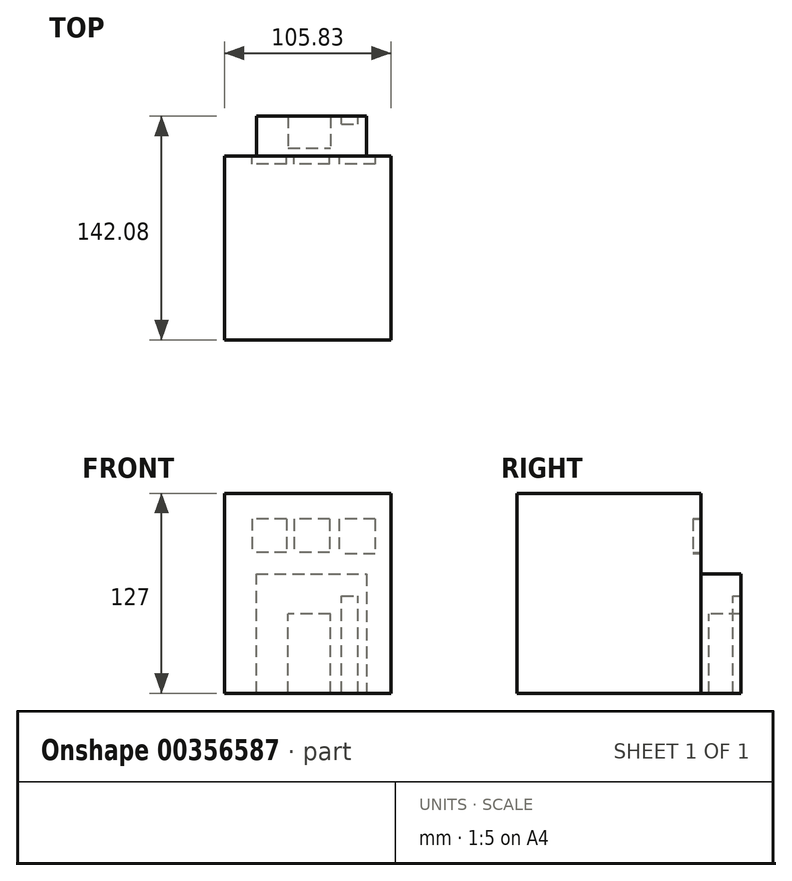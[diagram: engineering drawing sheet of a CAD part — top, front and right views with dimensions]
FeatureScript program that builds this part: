
annotation { "Feature Type Name" : "Feature", "Feature Type Description" : "" }
export const myFeature = defineFeature(function(context is Context, id is Id, definition is map)
    precondition{}
    {
        {
            var Q0;
            Q0=qCreatedBy(makeId("Top.planeOp"),FACE);
            var sketch = newSketch(context, id + "F0", { "sketchPlane" : qUnion([Q0])});
            skLineSegment(sketch, "E0.bottom", {"start": v(-52.34, 55.57) * mm, "end": v(53.5, 55.57) * mm});
            skLineSegment(sketch, "E0.top", {"start": v(-52.34, -56.03) * mm, "end": v(53.5, -56.03) * mm});
            skLineSegment(sketch, "E0.left", {"start": v(-52.34, 55.57) * mm, "end": v(-52.34, -56.03) * mm});
            skLineSegment(sketch, "E0.right", {"start": v(53.5, 55.57) * mm, "end": v(53.5, -56.03) * mm});
            skSolve(sketch);
        }
        {
            var Q0;
            Q0 = qSketchRegion(id + "F0", true);
            extrude(context, id + "F1", {"entities" : qUnion([Q0]), "depth" : 127 * mm});
        }
        {
            var Q0;
            Q0=makeQuery(id+"F1.opExtrude","SWEPT_FACE",FACE,{"disambiguationData":[OSD([sQuery(id+"F0.wireOp",EDGE,"E0.bottom")])]});
            var sketch = newSketch(context, id + "F2", { "sketchPlane" : qUnion([Q0])});
            skLineSegment(sketch, "E1.bottom", {"start": v(-43.27, 110.66) * mm, "end": v(-20.27, 110.66) * mm});
            skLineSegment(sketch, "E1.top", {"start": v(-43.27, 88.43) * mm, "end": v(-20.27, 88.43) * mm});
            skLineSegment(sketch, "E1.left", {"start": v(-43.27, 110.66) * mm, "end": v(-43.27, 88.43) * mm});
            skLineSegment(sketch, "E1.right", {"start": v(-20.27, 110.66) * mm, "end": v(-20.27, 88.43) * mm});
            skSolve(sketch);
        }
        {
            var Q0;
            Q0=makeQuery(id+"F2.imprint","IMPRINT",FACE,{"disambiguationData":[TD([[makeQuery(id+"F2.imprint","IMPRINT",EDGE,{"derivedFrom":sQuery(id+"F2.wireOp",EDGE,"E1.bottom")}),1.0]])]});
            extrude(context, id + "F3", {"entities" : qUnion([Q0]), "operationType" : NewBodyOperationType.ADD, "depth" : 5.08 * mm});
        }
        {
            var Q0;
            Q0=makeQuery(id+"F3.opExtrude","CAP_FACE",FACE,{"disambiguationData":[OSD([sQuery(id+"F0.wireOp",EDGE,"E0.bottom"),sQuery(id+"F0.wireOp",EDGE,"E0.left"),sQuery(id+"F0.wireOp",EDGE,"E0.right"),sQuery(id+"F2.wireOp",EDGE,"E1.bottom"),sQuery(id+"F2.wireOp",EDGE,"E1.top"),sQuery(id+"F2.wireOp",EDGE,"E1.left"),sQuery(id+"F2.wireOp",EDGE,"E1.right")])],"isStart":false});
            var sketch = newSketch(context, id + "F4", { "sketchPlane" : qUnion([Q0])});
            skLineSegment(sketch, "E2.bottom", {"start": v(-14.9, 0) * mm, "end": v(12.02, 0) * mm});
            skLineSegment(sketch, "E2.top", {"start": v(-14.9, 50.39) * mm, "end": v(12.02, 50.39) * mm});
            skLineSegment(sketch, "E2.left", {"start": v(-14.9, 0) * mm, "end": v(-14.9, 50.39) * mm});
            skLineSegment(sketch, "E2.right", {"start": v(12.02, 0) * mm, "end": v(12.02, 50.39) * mm});
            skSolve(sketch);
        }
        {
            var Q0;
            Q0=makeQuery(id+"F4.imprint","IMPRINT",FACE,{"disambiguationData":[TD([[makeQuery(id+"F4.imprint","IMPRINT",EDGE,{"derivedFrom":sQuery(id+"F4.wireOp",EDGE,"E2.bottom")}),-1.0]])]});
            extrude(context, id + "F5", {"entities" : qUnion([Q0]), "operationType" : NewBodyOperationType.ADD, "depth" : 5.08 * mm});
        }
        {
            var Q0;
            Q0=makeQuery(id+"F3.opExtrude","CAP_FACE",FACE,{"disambiguationData":[OSD([sQuery(id+"F0.wireOp",EDGE,"E0.bottom"),sQuery(id+"F0.wireOp",EDGE,"E0.left"),sQuery(id+"F0.wireOp",EDGE,"E0.right"),sQuery(id+"F2.wireOp",EDGE,"E1.bottom"),sQuery(id+"F2.wireOp",EDGE,"E1.top"),sQuery(id+"F2.wireOp",EDGE,"E1.left"),sQuery(id+"F2.wireOp",EDGE,"E1.right")])],"isStart":false});
            var sketch = newSketch(context, id + "F6", { "sketchPlane" : qUnion([Q0])});
            skLineSegment(sketch, "E3", {"start": v(-29.57, 0) * mm, "end": v(-29.57, 55.85) * mm});
            skLineSegment(sketch, "E4", {"start": v(-29.57, 55.85) * mm, "end": v(22.3, 55.85) * mm});
            skLineSegment(sketch, "E5", {"start": v(22.3, 55.85) * mm, "end": v(22.3, 0) * mm});
            skLineSegment(sketch, "E6", {"start": v(22.3, 0) * mm, "end": v(32.18, 0) * mm});
            skLineSegment(sketch, "E7", {"start": v(32.18, 0) * mm, "end": v(32.18, 75.75) * mm});
            skLineSegment(sketch, "E8", {"start": v(32.18, 75.75) * mm, "end": v(-37.89, 75.75) * mm});
            skLineSegment(sketch, "E9", {"start": v(-37.89, 75.75) * mm, "end": v(-37.89, 0) * mm});
            skSolve(sketch);
        }
        {
            var Q0;
            {var subQ0=sQuery(id+"F6.wireOp",EDGE,"E3");Q0=makeQuery(id+"F6.imprint","IMPRINT",FACE,{"disambiguationData":[TD([[makeQuery(id+"F6.imprint","IMPRINT",EDGE,{"derivedFrom":subQ0}),1.0]])]});}
            var Q1;
            {var subQ1=sQuery(id+"F6.wireOp",EDGE,"E3");Q1=makeQuery(id+"F6.imprint","IMPRINT",FACE,{"disambiguationData":[TD([[makeQuery(id+"F6.imprint","IMPRINT",EDGE,{"derivedFrom":subQ1}),-1.0]])]});}
            extrude(context, id + "F7", {"entities" : qUnion([Q0, Q1]), "operationType" : NewBodyOperationType.ADD, "depth" : 25.4 * mm});
        }
        {
            var Q0;
            Q0=makeQuery(id+"F3.opExtrude","CAP_FACE",FACE,{"disambiguationData":[OSD([sQuery(id+"F0.wireOp",EDGE,"E0.bottom"),sQuery(id+"F0.wireOp",EDGE,"E0.left"),sQuery(id+"F0.wireOp",EDGE,"E0.right"),sQuery(id+"F2.wireOp",EDGE,"E1.bottom"),sQuery(id+"F2.wireOp",EDGE,"E1.top"),sQuery(id+"F2.wireOp",EDGE,"E1.left"),sQuery(id+"F2.wireOp",EDGE,"E1.right")])],"isStart":false});
            var sketch = newSketch(context, id + "F8", { "sketchPlane" : qUnion([Q0])});
            skLineSegment(sketch, "E10.bottom", {"start": v(-14.4, 110.77) * mm, "end": v(8.1, 110.77) * mm});
            skLineSegment(sketch, "E10.top", {"start": v(-14.4, 89.38) * mm, "end": v(8.1, 89.38) * mm});
            skLineSegment(sketch, "E10.left", {"start": v(-14.4, 110.77) * mm, "end": v(-14.4, 89.38) * mm});
            skLineSegment(sketch, "E10.right", {"start": v(8.1, 110.77) * mm, "end": v(8.1, 89.38) * mm});
            skSolve(sketch);
        }
        {
            var Q0;
            Q0=makeQuery(id+"F8.imprint","IMPRINT",FACE,{"disambiguationData":[TD([[makeQuery(id+"F8.imprint","IMPRINT",EDGE,{"derivedFrom":sQuery(id+"F8.wireOp",EDGE,"E10.bottom")}),-1.0]])]});
            extrude(context, id + "F9", {"entities" : qUnion([Q0]), "operationType" : NewBodyOperationType.REMOVE, "oppositeDirection" : true, "depth" : 5.08 * mm});
        }
        {
            var Q0;
            Q0=makeQuery(id+"F3.opExtrude","CAP_FACE",FACE,{"disambiguationData":[OSD([sQuery(id+"F0.wireOp",EDGE,"E0.bottom"),sQuery(id+"F0.wireOp",EDGE,"E0.left"),sQuery(id+"F0.wireOp",EDGE,"E0.right"),sQuery(id+"F2.wireOp",EDGE,"E1.bottom"),sQuery(id+"F2.wireOp",EDGE,"E1.top"),sQuery(id+"F2.wireOp",EDGE,"E1.left"),sQuery(id+"F2.wireOp",EDGE,"E1.right")])],"isStart":false});
            var sketch = newSketch(context, id + "F10", { "sketchPlane" : qUnion([Q0])});
            skLineSegment(sketch, "E11.bottom", {"start": v(13, 110.85) * mm, "end": v(35.02, 110.85) * mm});
            skLineSegment(sketch, "E11.top", {"start": v(13, 89.38) * mm, "end": v(35.02, 89.38) * mm});
            skLineSegment(sketch, "E11.left", {"start": v(13, 110.85) * mm, "end": v(13, 89.38) * mm});
            skLineSegment(sketch, "E11.right", {"start": v(35.02, 110.85) * mm, "end": v(35.02, 89.38) * mm});
            skSolve(sketch);
        }
        {
            var Q0;
            Q0 = qSketchRegion(id + "F10", true);
            extrude(context, id + "F11", {"entities" : qUnion([Q0]), "operationType" : NewBodyOperationType.REMOVE, "oppositeDirection" : true, "depth" : 5.08 * mm});
        }
        {
            var Q0;
            Q0=makeQuery(id+"F7.opExtrude","CAP_FACE",FACE,{"disambiguationData":[OSD([sQuery(id+"F0.wireOp",EDGE,"E0.bottom"),sQuery(id+"F4.wireOp",EDGE,"E2.top"),sQuery(id+"F4.wireOp",EDGE,"E2.left"),sQuery(id+"F4.wireOp",EDGE,"E2.right"),sQuery(id+"F6.wireOp",EDGE,"E6"),sQuery(id+"F6.wireOp",EDGE,"E7"),sQuery(id+"F6.wireOp",EDGE,"E8"),sQuery(id+"F6.wireOp",EDGE,"E9")])],"isStart":false});
            var sketch = newSketch(context, id + "F12", { "sketchPlane" : qUnion([Q0])});
            skLineSegment(sketch, "E12.bottom", {"start": v(-22.02, 0) * mm, "end": v(-32.3, 0) * mm});
            skLineSegment(sketch, "E12.top", {"start": v(-22.02, 61.8) * mm, "end": v(-32.3, 61.8) * mm});
            skLineSegment(sketch, "E12.left", {"start": v(-22.02, 0) * mm, "end": v(-22.02, 61.8) * mm});
            skLineSegment(sketch, "E12.right", {"start": v(-32.3, 0) * mm, "end": v(-32.3, 61.8) * mm});
            skSolve(sketch);
        }
        {
            var Q0;
            Q0 = qSketchRegion(id + "F12", true);
            extrude(context, id + "F13", {"entities" : qUnion([Q0]), "operationType" : NewBodyOperationType.REMOVE, "oppositeDirection" : true, "depth" : 5.08 * mm});
        }
    });
